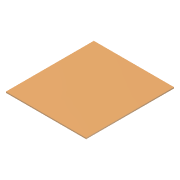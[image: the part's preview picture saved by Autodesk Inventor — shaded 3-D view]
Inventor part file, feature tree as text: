
AUTODESK INVENTOR PART (.ipt)
format: ipt  version: 2014 (Build 180170000, 170)  size: 78,848 bytes
history: native  units: mm
features: extrude x1, sketch x1
ambient origin geometry x8: Origin, YZ Plane, XZ Plane, XY Plane, X Axis, Y Axis, Z Axis, Center Point
bodies: Solid1 (feature_tree)
feature tree (2):
  extrude  "Extrusion1"  Depth=210.0mm
  sketch  "Sketch1"  dims[d0=230.0mm d1=210.0mm d2=3.0mm d3=0.0mm]
